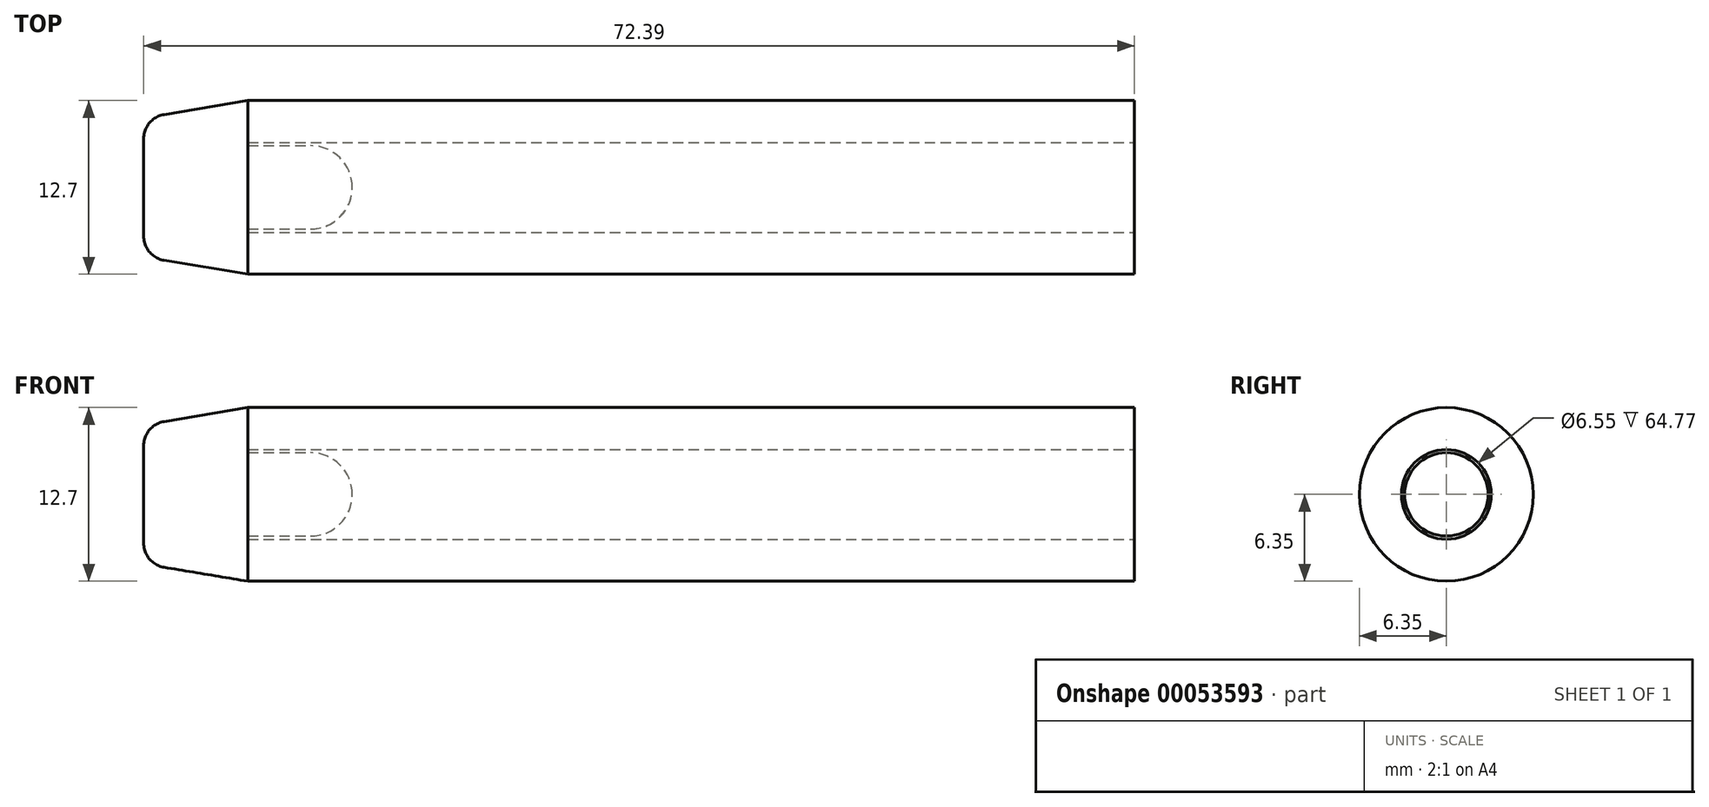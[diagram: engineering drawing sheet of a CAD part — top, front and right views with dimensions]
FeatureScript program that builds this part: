
annotation { "Feature Type Name" : "Feature", "Feature Type Description" : "" }
export const myFeature = defineFeature(function(context is Context, id is Id, definition is map)
    precondition{}
    {
        {
            var Q0;
            Q0=qCreatedBy(makeId("Top.planeOp"),FACE);
            var sketch = newSketch(context, id + "F0", { "sketchPlane" : qUnion([Q0])});
            skLineSegment(sketch, "E0.bottom", {"start": v(0, 6.35) * mm, "end": v(64.77, 6.35) * mm});
            skLineSegment(sketch, "E0.top", {"start": v(0, 3.28) * mm, "end": v(64.77, 3.28) * mm});
            skLineSegment(sketch, "E0.left", {"start": v(0, 6.35) * mm, "end": v(0, 3.28) * mm});
            skLineSegment(sketch, "E0.right", {"start": v(64.77, 6.35) * mm, "end": v(64.77, 3.28) * mm});
            skSolve(sketch);
        }
        {
            var Q0;
            Q0=qCreatedBy(makeId("Top.planeOp"),FACE);
            var sketch = newSketch(context, id + "F1", { "sketchPlane" : qUnion([Q0])});
            skLineSegment(sketch, "E1", {"start": v(0, 3.05) * mm, "end": v(4.57, 3.05) * mm});
            skLineSegment(sketch, "E2", {"start": v(7.62, 0) * mm, "end": v(7.62, 0) * mm});
            skLineSegment(sketch, "E3", {"start": v(7.62, 0) * mm, "end": v(-7.62, 0) * mm});
            skLineSegment(sketch, "E4", {"start": v(-7.62, 0) * mm, "end": v(-7.62, 3.57) * mm});
            skLineSegment(sketch, "E5", {"start": v(0, 6.35) * mm, "end": v(0, 3.05) * mm});
            skLineSegment(sketch, "E6", {"start": v(-6.13, 5.33) * mm, "end": v(0, 6.35) * mm});
            skLineSegment(sketch, "E7.right", {"start": v(69.77, 2.6) * mm, "end": v(69.77, -0.47) * mm});
            skPoint(sketch, "E8.visualSharp", {"position": v(7.62, 3.05) * mm});
            skArc(sketch, "E8.filletArc", {"start": v(7.62, 0) * mm, "mid": v(6.73, 2.16) * mm, "end": v(4.57, 3.05) * mm});
            skPoint(sketch, "E9.visualSharp", {"position": v(-7.62, 5.08) * mm});
            skArc(sketch, "E9.filletArc", {"start": v(-6.13, 5.33) * mm, "mid": v(-7.2, 4.72) * mm, "end": v(-7.62, 3.57) * mm});
            skPoint(sketch, "E10.visualSharp", {"position": v(0, 6.35) * mm});
            skSolve(sketch);
        }
        {
            var Q0;
            Q0=makeQuery(id+"F0.imprint","IMPRINT",FACE,{"disambiguationData":[TD([[makeQuery(id+"F0.imprint","IMPRINT",EDGE,{"derivedFrom":sQuery(id+"F0.wireOp",EDGE,"E0.bottom")}),-1.0]])]});
            var Q1;
            Q1 = qSketchRegion(id + "F0", true);
            var Q2;
            Q2=sQuery(id+"F1.wireOp",EDGE,"E3");
            revolve(context, id + "F2", {"entities" : qUnion([Q0, Q1]), "axis" : qUnion([Q2]), "revolveType" : RevolveType.FULL});
        }
        {
            var Q0;
            Q0 = qSketchRegion(id + "F1", true);
            var Q1;
            Q1=sQuery(id+"F1.wireOp",EDGE,"E3");
            revolve(context, id + "F3", {"operationType" : NewBodyOperationType.ADD, "entities" : qUnion([Q0]), "axis" : qUnion([Q1]), "revolveType" : RevolveType.FULL});
        }
    });
